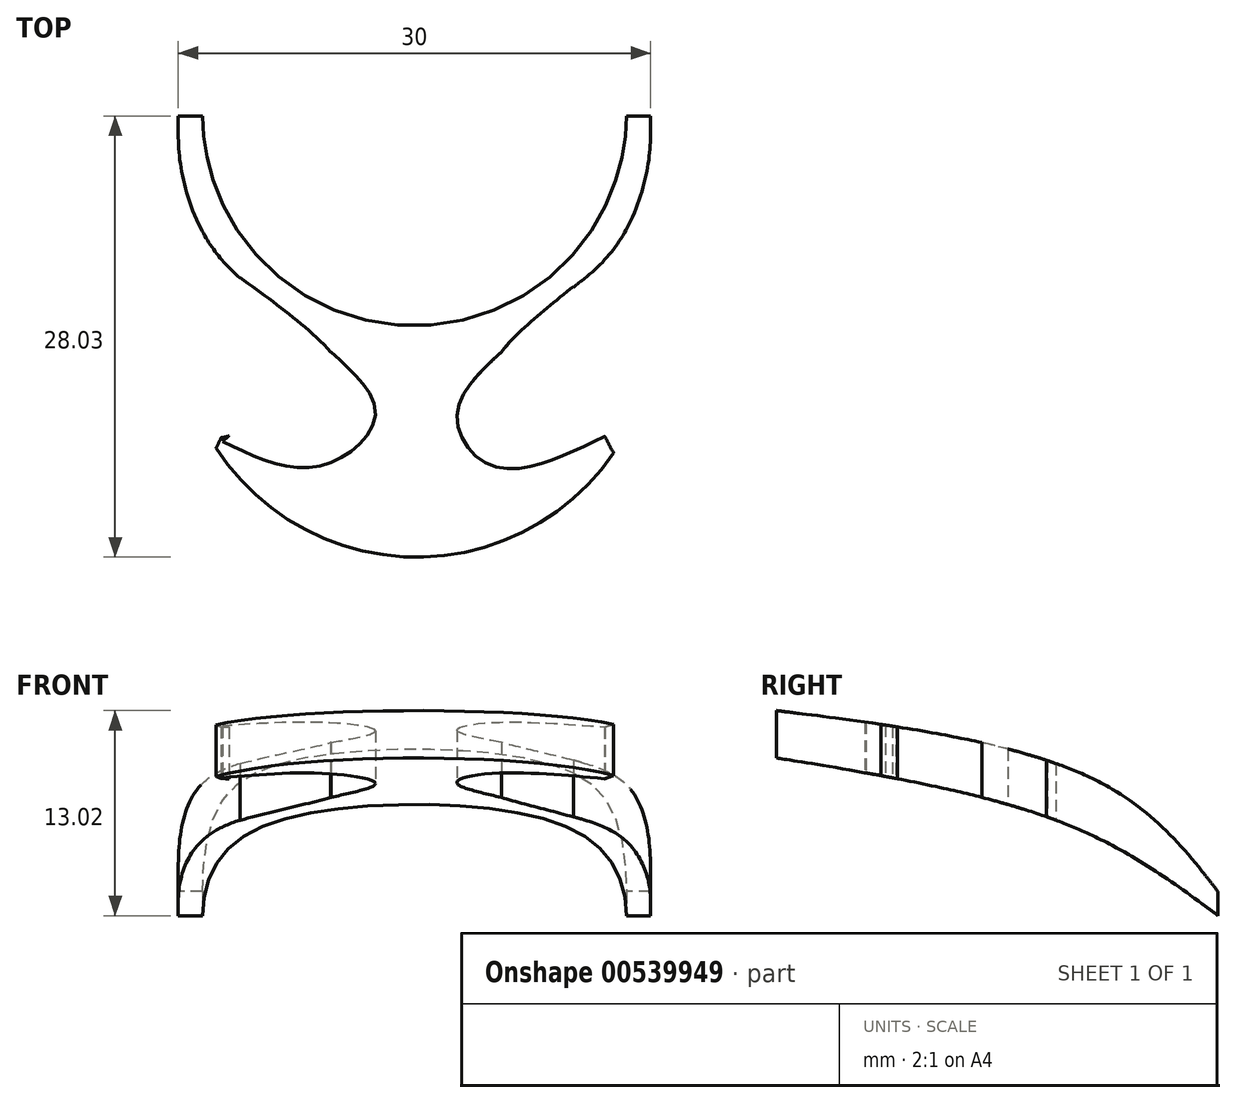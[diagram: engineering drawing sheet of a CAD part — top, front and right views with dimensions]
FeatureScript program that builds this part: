
annotation { "Feature Type Name" : "Feature", "Feature Type Description" : "" }
export const myFeature = defineFeature(function(context is Context, id is Id, definition is map)
    precondition{}
    {
        {
            var Q0;
            Q0=qCreatedBy(makeId("Top.planeOp"),FACE);
            var sketch = newSketch(context, id + "F0", { "sketchPlane" : qUnion([Q0])});
            skLineSegment(sketch, "E0.bottom", {"start": v(15, -15) * mm, "end": v(-15, -15) * mm});
            skLineSegment(sketch, "E0.top", {"start": v(15, 15) * mm, "end": v(-15, 15) * mm});
            skLineSegment(sketch, "E0.left", {"start": v(15, -15) * mm, "end": v(15, 15) * mm});
            skLineSegment(sketch, "E0.right", {"start": v(-15, -15) * mm, "end": v(-15, 15) * mm});
            skPoint(sketch, "E0.middle", {"position": v(0, 0) * mm});
            skSolve(sketch);
        }
        {
            var Q0;
            Q0=makeQuery(id+"F0.imprint","IMPRINT",FACE,{"disambiguationData":[TD([[makeQuery(id+"F0.imprint","IMPRINT",EDGE,{"derivedFrom":sQuery(id+"F0.wireOp",EDGE,"E0.bottom")}),-1.0]])]});
            extrude(context, id + "F1", {"entities" : qUnion([Q0]), "depth" : 15 * mm, "offsetDistance" : 25 * mm});
        }
        {
            var Q0;
            Q0=makeQuery(id+"F1.opExtrude","SWEPT_FACE",FACE,{"disambiguationData":[OSD([sQuery(id+"F0.wireOp",EDGE,"E0.right")])]});
            var sketch = newSketch(context, id + "F2", { "sketchPlane" : qUnion([Q0])});
            skFitSpline(sketch, "E1", {"points": [v(-15, 0) * mm, v(-5.4, 5.8) * mm, v(15, 10.33) * mm], "startDerivative": vector(20.04, 14.95) * mm, "endDerivative": vector(38.99, 6.16) * mm});
            skFitSpline(sketch, "E2", {"points": [v(-15, 1.53) * mm, v(-7.53, 8.46) * mm, v(15, 13.26) * mm], "startDerivative": vector(14.95, 19.22) * mm, "endDerivative": vector(43.16, 5.18) * mm});
            skLineSegment(sketch, "E3", {"start": v(-15, 1.53) * mm, "end": v(-15, 0) * mm});
            skLineSegment(sketch, "E4", {"start": v(15, 13.26) * mm, "end": v(15, 10.33) * mm});
            skSolve(sketch);
        }
        {
            var Q0;
            {var subQ0=sQuery(id+"F2.wireOp",EDGE,"E2");Q0=makeQuery(id+"F2.imprint","IMPRINT",FACE,{"disambiguationData":[TD([[makeQuery(id+"F2.imprint","IMPRINT",EDGE,{"derivedFrom":subQ0}),1.0]])]});}
            var Q1;
            {var subQ0=sQuery(id+"F2.wireOp",EDGE,"E1");Q1=makeQuery(id+"F2.imprint","IMPRINT",FACE,{"disambiguationData":[TD([[makeQuery(id+"F2.imprint","IMPRINT",EDGE,{"derivedFrom":subQ0}),-1.0]])]});}
            extrude(context, id + "F3", {"entities" : qUnion([Q0, Q1]), "operationType" : NewBodyOperationType.REMOVE, "oppositeDirection" : true, "depth" : 100.1 * mm, "offsetDistance" : 25 * mm});
        }
        {
            var Q0;
            Q0=qCreatedBy(makeId("Top.planeOp"),FACE);
            var sketch = newSketch(context, id + "F4", { "sketchPlane" : qUnion([Q0])});
            skCircle(sketch, "E5", {"center": v(0, 15.12) * mm, "radius": 13.46 * mm});
            skSolve(sketch);
        }
        {
            var Q0;
            Q0 = qSketchRegion(id + "F4", true);
            extrude(context, id + "F5", {"entities" : qUnion([Q0]), "operationType" : NewBodyOperationType.REMOVE, "depth" : 21.6 * mm, "offsetDistance" : 25 * mm});
        }
        {
            var Q0;
            Q0=qCreatedBy(makeId("Top.planeOp"),FACE);
            var sketch = newSketch(context, id + "F6", { "sketchPlane" : qUnion([Q0])});
            skArc(sketch, "E6", {"start": v(-14.89, 0) * mm, "mid": v(0.13, -13.03) * mm, "end": v(15.14, 0) * mm});
            skLineSegment(sketch, "E7", {"start": v(15.14, 0) * mm, "end": v(22.35, -19.57) * mm});
            skLineSegment(sketch, "E8", {"start": v(22.35, -19.57) * mm, "end": v(-18.28, -24.05) * mm});
            skLineSegment(sketch, "E9", {"start": v(-18.28, -24.05) * mm, "end": v(-21.27, -1.36) * mm});
            skLineSegment(sketch, "E10", {"start": v(-21.27, -1.36) * mm, "end": v(-14.89, 0) * mm});
            skSolve(sketch);
        }
        {
            var Q0;
            Q0 = qSketchRegion(id + "F6", true);
            extrude(context, id + "F7", {"entities" : qUnion([Q0]), "operationType" : NewBodyOperationType.REMOVE, "depth" : 47 * mm, "offsetDistance" : 25 * mm});
        }
        {
            var Q0;
            Q0=qCreatedBy(makeId("Top.planeOp"),FACE);
            var sketch = newSketch(context, id + "F8", { "sketchPlane" : qUnion([Q0])});
            skCircle(sketch, "E11", {"center": v(-24.53, 0) * mm, "radius": 13.4 * mm});
            skCircle(sketch, "E12", {"center": v(23.58, 0) * mm, "radius": 12.67 * mm});
            skSolve(sketch);
        }
        {
            var Q0;
            Q0 = qSketchRegion(id + "F8", true);
            extrude(context, id + "F9", {"entities" : qUnion([Q0]), "operationType" : NewBodyOperationType.REMOVE, "depth" : 42.1 * mm, "offsetDistance" : 25 * mm});
        }
        {
            var Q0;
            Q0=makeQuery(id+"F9.boolean.opBoolean","INTERSECT",EDGE,{"derivedFrom":[makeQuery(id+"F1.opExtrude","SWEPT_FACE",FACE,{"disambiguationData":[OSD([sQuery(id+"F0.wireOp",EDGE,"E0.right")])]}),makeQuery(id+"F9.opExtrude","SWEPT_FACE",FACE,{"disambiguationData":[OSD([sQuery(id+"F8.wireOp",EDGE,"E11")])]})]});
            var Q1;
            Q1=makeQuery(id+"F9.boolean.opBoolean","INTERSECT",EDGE,{"derivedFrom":[makeQuery(id+"F1.opExtrude","SWEPT_FACE",FACE,{"disambiguationData":[OSD([sQuery(id+"F0.wireOp",EDGE,"E0.left")])]}),makeQuery(id+"F9.opExtrude","SWEPT_FACE",FACE,{"disambiguationData":[OSD([sQuery(id+"F8.wireOp",EDGE,"E12")])]})]});
            fillet(context, id + "F10", {"entities" : qUnion([Q0, Q1]), "radius" : 13.3 * mm, "tangentPropagation" : true, "allowEdgeOverflow" : false});
        }
        {
            var Q0;
            Q0=qCreatedBy(makeId("Top.planeOp"),FACE);
            var sketch = newSketch(context, id + "F11", { "sketchPlane" : qUnion([Q0])});
            skCircle(sketch, "E13", {"center": v(13.93, 0) * mm, "radius": 5.61 * mm});
            skCircle(sketch, "E14", {"center": v(-14.74, 0) * mm, "radius": 5.96 * mm});
            skSolve(sketch);
        }
        {
            var Q0;
            Q0 = qSketchRegion(id + "F11", true);
            extrude(context, id + "F12", {"entities" : qUnion([Q0]), "operationType" : NewBodyOperationType.REMOVE, "depth" : 29.7 * mm, "offsetDistance" : 25 * mm});
        }
        {
            var Q0;
            Q0=makeQuery(id+"F12.boolean.opBoolean","INTERSECT",EDGE,{"disambiguationData":[OD(1.0)],"derivedFrom":[makeQuery(id+"F9.boolean.opBoolean","COPY",FACE,{"derivedFrom":makeQuery(id+"F9.opExtrude","SWEPT_FACE",FACE,{"disambiguationData":[OSD([sQuery(id+"F8.wireOp",EDGE,"E11")])]})}),makeQuery(id+"F12.opExtrude","SWEPT_FACE",FACE,{"disambiguationData":[OSD([sQuery(id+"F11.wireOp",EDGE,"E14")])]})]});
            fillet(context, id + "F13", {"entities" : qUnion([Q0]), "radius" : 10 * mm, "tangentPropagation" : true, "allowEdgeOverflow" : false});
        }
        {
            var Q0;
            Q0=makeQuery(id+"F12.boolean.opBoolean","INTERSECT",EDGE,{"disambiguationData":[OD(1.0)],"derivedFrom":[makeQuery(id+"F9.boolean.opBoolean","COPY",FACE,{"derivedFrom":makeQuery(id+"F9.opExtrude","SWEPT_FACE",FACE,{"disambiguationData":[OSD([sQuery(id+"F8.wireOp",EDGE,"E12")])]})}),makeQuery(id+"F12.opExtrude","SWEPT_FACE",FACE,{"disambiguationData":[OSD([sQuery(id+"F11.wireOp",EDGE,"E13")])]})]});
            fillet(context, id + "F14", {"entities" : qUnion([Q0]), "radius" : 10 * mm, "tangentPropagation" : true, "allowEdgeOverflow" : false});
        }
        {
            var Q0;
            Q0=qCreatedBy(makeId("Top.planeOp"),FACE);
            var sketch = newSketch(context, id + "F15", { "sketchPlane" : qUnion([Q0])});
            skFitSpline(sketch, "E15", {"points": [v(-11.08, 4.72) * mm, v(-4.5, -1.98) * mm, v(-12.24, -5.45) * mm], "startDerivative": vector(20.2, -14.6) * mm, "endDerivative": vector(-22.87, -5.67) * mm});
            skFitSpline(sketch, "E16", {"points": [v(10.1, 4.16) * mm, v(4.79, -1.98) * mm, v(12.09, -5.37) * mm], "startDerivative": vector(-16.9, -13.63) * mm, "endDerivative": vector(20.92, -5.43) * mm});
            skLineSegment(sketch, "E17", {"start": v(-11.08, 4.72) * mm, "end": v(-12.24, -5.45) * mm});
            skLineSegment(sketch, "E18", {"start": v(10.1, 4.16) * mm, "end": v(12.09, -5.37) * mm});
            skSolve(sketch);
        }
        {
            var Q0;
            Q0 = qSketchRegion(id + "F15", true);
            extrude(context, id + "F16", {"entities" : qUnion([Q0]), "operationType" : NewBodyOperationType.REMOVE, "depth" : 25.6 * mm, "offsetDistance" : 25 * mm});
        }
        {
            var Q0;
            Q0=qCreatedBy(makeId("Top.planeOp"),FACE);
            var sketch = newSketch(context, id + "F17", { "sketchPlane" : qUnion([Q0])});
            skFitSpline(sketch, "E19", {"points": [v(-5.3, 0) * mm, v(-2.48, -4.02) * mm, v(-6.07, -7.26) * mm, v(-12.19, -5.67) * mm], "startDerivative": vector(13.84, -12.3) * mm, "endDerivative": vector(-17.01, 8.34) * mm});
            skFitSpline(sketch, "E20", {"points": [v(5.52, 0) * mm, v(2.7, -4.02) * mm, v(5.05, -7.26) * mm, v(12.16, -5.32) * mm], "startDerivative": vector(-12.94, -12.02) * mm, "endDerivative": vector(19.98, 9.76) * mm});
            skLineSegment(sketch, "E21", {"start": v(-5.3, 0) * mm, "end": v(-12.19, -5.67) * mm});
            skLineSegment(sketch, "E22", {"start": v(5.52, 0) * mm, "end": v(12.16, -5.32) * mm});
            skSolve(sketch);
        }
        {
            var Q0;
            Q0 = qSketchRegion(id + "F17", true);
            extrude(context, id + "F18", {"entities" : qUnion([Q0]), "operationType" : NewBodyOperationType.REMOVE, "depth" : 30.1 * mm, "offsetDistance" : 25 * mm});
        }
    });
